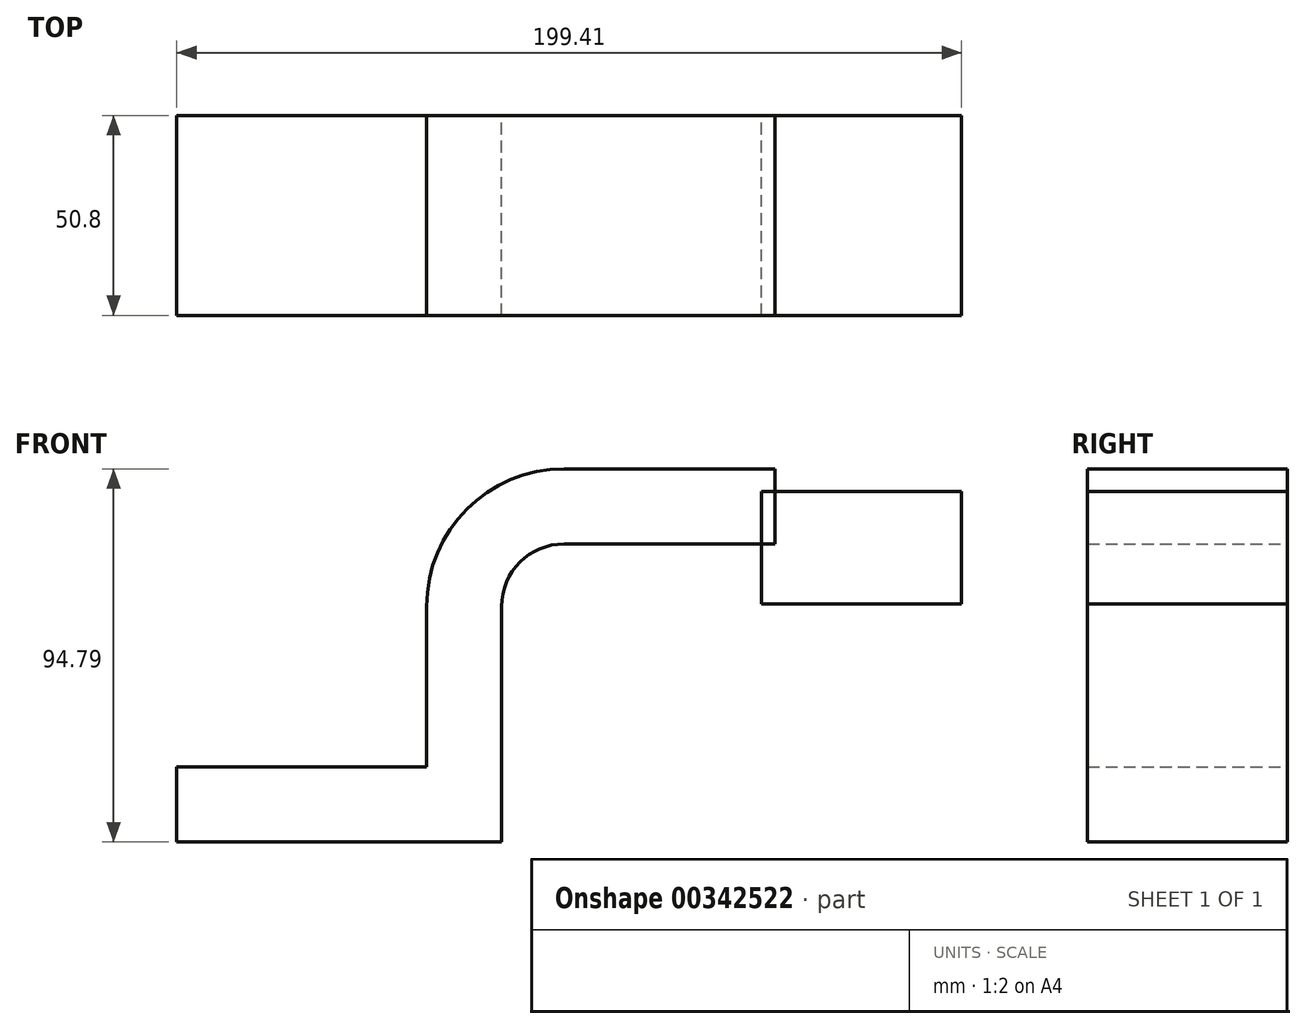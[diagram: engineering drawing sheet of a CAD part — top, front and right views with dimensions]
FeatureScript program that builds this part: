
annotation { "Feature Type Name" : "Feature", "Feature Type Description" : "" }
export const myFeature = defineFeature(function(context is Context, id is Id, definition is map)
    precondition{}
    {
        {
            var Q0;
            Q0=qCreatedBy(makeId("Front.planeOp"),FACE);
            var sketch = newSketch(context, id + "F0", { "sketchPlane" : qUnion([Q0])});
            skLineSegment(sketch, "E0.bottom", {"start": v(41.27, 9.53) * mm, "end": v(-41.28, 9.53) * mm});
            skLineSegment(sketch, "E0.top", {"start": v(41.28, -9.52) * mm, "end": v(-41.27, -9.52) * mm});
            skLineSegment(sketch, "E0.left", {"start": v(41.28, 9.53) * mm, "end": v(41.28, -9.52) * mm});
            skLineSegment(sketch, "E0.right", {"start": v(-41.28, 9.53) * mm, "end": v(-41.27, -9.52) * mm});
            skPoint(sketch, "E0.middle", {"position": v(0, 0) * mm});
            skLineSegment(sketch, "E1.bottom", {"start": v(107.34, 51) * mm, "end": v(158.14, 51) * mm});
            skLineSegment(sketch, "E1.top", {"start": v(107.34, 79.58) * mm, "end": v(158.14, 79.58) * mm});
            skLineSegment(sketch, "E1.left", {"start": v(107.34, 51) * mm, "end": v(107.34, 79.58) * mm});
            skLineSegment(sketch, "E1.right", {"start": v(158.14, 51) * mm, "end": v(158.14, 79.58) * mm});
            skPoint(sketch, "E1.middle", {"position": v(132.74, 65.3) * mm});
            skLineSegment(sketch, "E2", {"start": v(41.27, 9.53) * mm, "end": v(41.27, 50.33) * mm});
            skArc(sketch, "E3", {"start": v(41.27, 50.33) * mm, "mid": v(45.92, 61.56) * mm, "end": v(57.15, 66.2) * mm});
            skLineSegment(sketch, "E4", {"start": v(57.15, 66.2) * mm, "end": v(110.73, 66.2) * mm});
            skLineSegment(sketch, "E5.0", {"start": v(57.15, 85.26) * mm, "end": v(110.73, 85.26) * mm});
            skArc(sketch, "E5.1", {"start": v(22.23, 50.33) * mm, "mid": v(32.45, 75.03) * mm, "end": v(57.15, 85.26) * mm});
            skLineSegment(sketch, "E5.2", {"start": v(22.22, 9.53) * mm, "end": v(22.22, 50.33) * mm});
            skLineSegment(sketch, "E6", {"start": v(110.73, 85.26) * mm, "end": v(110.73, 66.2) * mm});
            skFitSpline(sketch, "E7", {"points": [v(-41.28, 9.52) * mm, v(57.15, 85.26) * mm], "startDerivative": vector(-74.6, 133.18) * mm, "endDerivative": vector(119.76, -48.05) * mm});
            skSolve(sketch);
        }
        {
            var Q0;
            Q0=makeQuery(id+"F0.imprint","IMPRINT",FACE,{"disambiguationData":[TD([[makeQuery(id+"F0.imprint","IMPRINT",EDGE,{"derivedFrom":sQuery(id+"F0.wireOp",EDGE,"E5.1")}),1.0]])]});
            var Q1;
            {var subQ1=sQuery(id+"F0.wireOp",EDGE,"E1.bottom");Q1=makeQuery(id+"F0.imprint","IMPRINT",FACE,{"disambiguationData":[TD([[makeQuery(id+"F0.imprint","IMPRINT",EDGE,{"derivedFrom":subQ1}),1.0]])]});}
            var Q2;
            Q2=makeQuery(id+"F0.imprint","IMPRINT",FACE,{"disambiguationData":[TD([[makeQuery(id+"F0.imprint","IMPRINT",EDGE,{"derivedFrom":sQuery(id+"F0.wireOp",EDGE,"E0.top")}),-1.0]])]});
            var Q3;
            {var subQ5=sQuery(id+"F0.wireOp",EDGE,"E2");Q3=makeQuery(id+"F0.imprint","IMPRINT",FACE,{"disambiguationData":[TD([[makeQuery(id+"F0.imprint","IMPRINT",EDGE,{"derivedFrom":subQ5}),1.0]])]});}
            extrude(context, id + "F1", {"entities" : qUnion([Q0, Q1, Q2, Q3]), "endBound" : BoundingType.SYMMETRIC, "depth" : 50.8 * mm});
        }
    });
